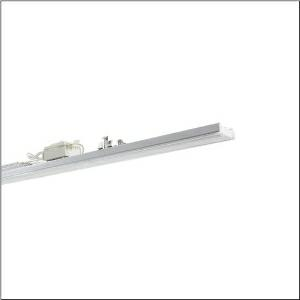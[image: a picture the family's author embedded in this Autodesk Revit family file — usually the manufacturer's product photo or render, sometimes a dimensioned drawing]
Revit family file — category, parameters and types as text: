
# Revit family: licross_r__21_recessed_mo_52te12dn455g_92c8
name_source: partatom
category: Lighting Fixtures
units: mm (PartAtom-declared; Revit-internal decimal feet)

## family parameters
Cut with Voids When Loaded = No
Host = Face
Light Source = No
Part Type = Normal
Room Calculation Point = No
Round Connector Dimension = Use Diameter
Shared = No

## types (1)
- --- (1 x LED, 5510 lm, 29.7 W, 4000K)
    Apparent Load = 30 VA
    CIE Flux Codes = 72 92 99 100 100
    Color Rendering = 80
    Color Temperature = 4000K
    Default Elevation = 1800 mm
    Description = Licross® 21 Recessed MO, luminaire insert, of sheet steel, galvanised, coil coated, white, length: 1.500mm, width: 66mm, height: 67mm, LED rated luminous flux: 5.510lm, light colour: 840, control gear: DALI 2, with plug, 5-pole, with phase selection, mains connection: 220..240V, AC, 50/60Hz, rated input power: 30W, internal wiring halogen-free, primary optical cover: cover, of PMMA, light emission: direct distribution, primary light characteristic: symmetric, protection rating (complete): IP54, insulation class (complete): insulation class I (protective earthing), certification: CE, ENEC, VDE, UKCA, protection symbol: D if used in an environment with non-conductive dust loads with corresponding accessories, impact resistance: IK06, permissible ambient temperature for indoor applications: -25..+45°C, corresponds to IFS (International Featured Standards) requirements for safety and quality in the food industry, reducing of maximum allowable ambient temperature of 5°C with ceiling mounting, LABS conformity tested according to VDMA 24364:2018-05, packaging unit: 1 piece
    Height = 58 mm
    Lamp = 1 x LED
    Lamp Light Flux = 5510 lm
    Lamp Power = 29.7 W
    Lamp count = 1
    Length = 1500 mm
    Luminous efficacy = 186 lm/W
    Manufacturer = Siteco
    ModVariant = No
    Model = 52TE12DN455G
    Mounting Place = Ceiling
    Mounting Type = Pendant
    Number of Poles = 1
    OnlyDefault = Yes
    Power Factor = 1
    Product Name = Licross® 21 Recessed MO
    Product group = luminaire insert | ceiling pendant
    ProductGroupID = 902
    Protection Class = Protection class I
    Protection Degree = IP 54
    RLX_Detail_Level = 1
    RLX_Emergency_Light_Flux = 0 lm
    RLX_Emergency_Type = 0
    RLX_Emergency_Type_DB = No
    RlxData = <blob elided: 24001 chars, md5=fd82b402>
    Socket = socket
    Standby Power = 0 W
    System Light Flux = 5510 lm
    System Power = 30 W
    Type Comments = factory setting: luminous flux: 100 % | dim-lin: 254 | 201 mA
    Type Image = l_1296930.jpg
    URL = http://relux.com
    VarID = @adj_101377
    Voltage = 0 V
    Weight = 0.00 kg
    Width = 66 mm

## geometry (parser evidence)
native form markers: Blend x4, Sweep x11
no freeform markers — native parametric forms only
